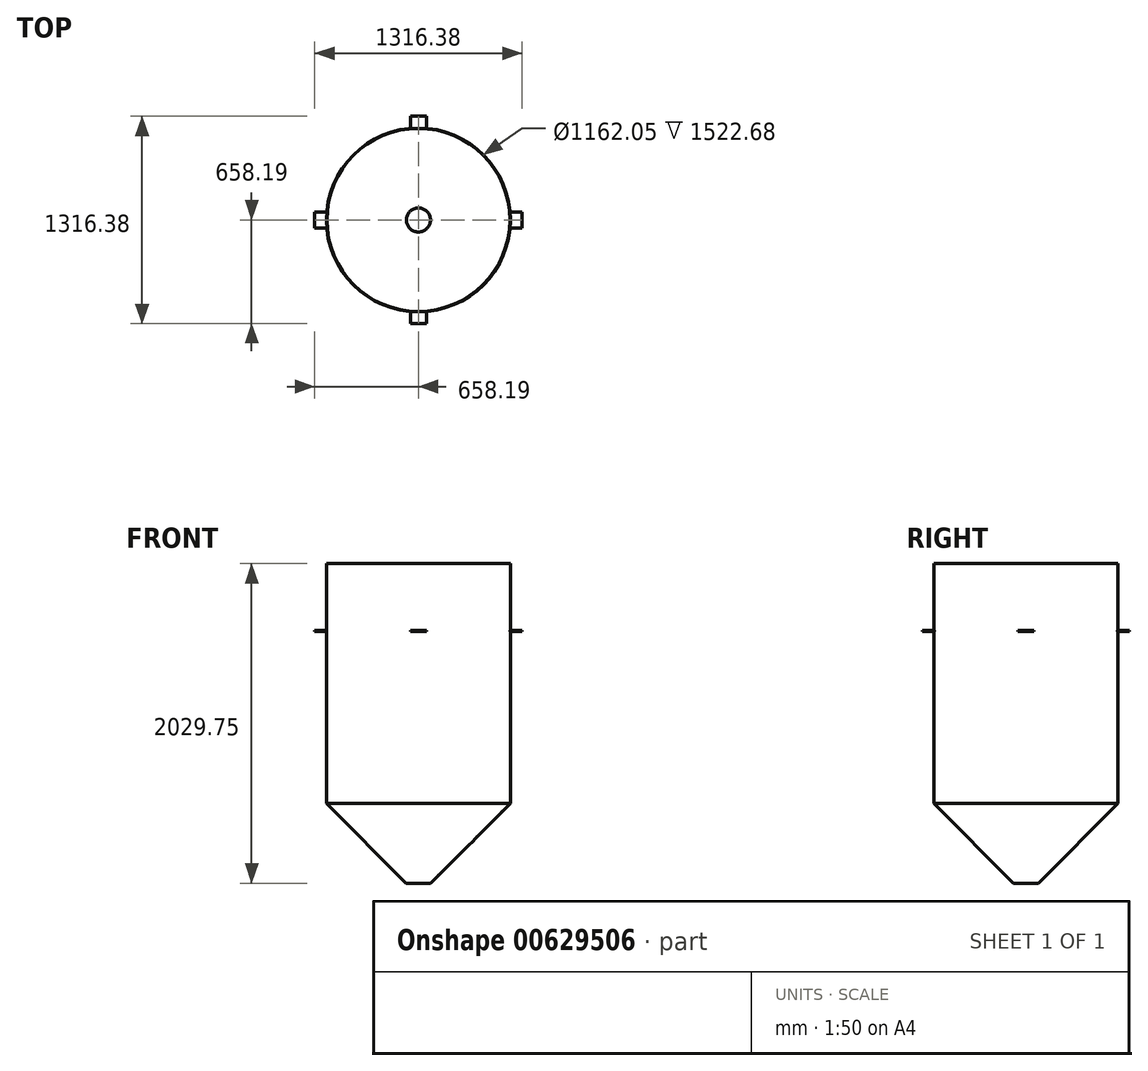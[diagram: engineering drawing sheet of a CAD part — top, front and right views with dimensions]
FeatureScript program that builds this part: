
annotation { "Feature Type Name" : "Feature", "Feature Type Description" : "" }
export const myFeature = defineFeature(function(context is Context, id is Id, definition is map)
    precondition{}
    {
        {
            var Q0;
            Q0=qCreatedBy(makeId("Right.planeOp"),FACE);
            var sketch = newSketch(context, id + "F0", { "sketchPlane" : qUnion([Q0])});
            skLineSegment(sketch, "E0", {"start": v(-584.2, 1524) * mm, "end": v(-584.2, 0) * mm});
            skLineSegment(sketch, "E1", {"start": v(-584.2, 0) * mm, "end": v(-78.45, -505.75) * mm});
            skLineSegment(sketch, "E2", {"start": v(-78.45, -505.75) * mm, "end": v(-76.2, -503.5) * mm});
            skLineSegment(sketch, "E3", {"start": v(-581.02, 1.32) * mm, "end": v(-581.02, 1524) * mm});
            skLineSegment(sketch, "E4", {"start": v(-581.02, 1524) * mm, "end": v(-584.2, 1524) * mm});
            skLineSegment(sketch, "E5", {"start": v(0, 139.51) * mm, "end": v(0, -139.51) * mm, "construction": true});
            skLineSegment(sketch, "E6", {"start": v(-76.2, -503.5) * mm, "end": v(-581.02, 1.32) * mm});
            skLineSegment(sketch, "E7", {"start": v(-78.45, -505.75) * mm, "end": v(0, -584.2) * mm, "construction": true});
            skSolve(sketch);
        }
        {
            var Q0;
            Q0=qSketchRegion(id+"F0",true);
            var Q1;
            Q1=sQuery(id+"F0.wireOp",EDGE,"E5");
            revolve(context, id + "F1", {"entities" : qUnion([Q0]), "axis" : qUnion([Q1]), "revolveType" : RevolveType.FULL});
        }
        {
            var Q0;
            Q0=qCreatedBy(makeId("Top.planeOp"),FACE);
            cPlane(context, id + "F2", {"entities" : qUnion([Q0]), "cplaneType" : CPlaneType.OFFSET, "offset" : 1092.2 * mm, "width" : 152.4 * mm, "height" : 152.4 * mm});
        }
        {
            var Q0;
            Q0=qCreatedBy(id+"F2.planeOp",FACE);
            var sketch = newSketch(context, id + "F3", { "sketchPlane" : qUnion([Q0])});
            skLineSegment(sketch, "E8.bottom", {"start": v(-50.8, 658.19) * mm, "end": v(50.8, 658.19) * mm});
            skLineSegment(sketch, "E8.top", {"start": v(-50.8, 581.99) * mm, "end": v(50.8, 581.99) * mm});
            skLineSegment(sketch, "E8.left", {"start": v(-50.8, 658.19) * mm, "end": v(-50.8, 581.99) * mm});
            skLineSegment(sketch, "E8.right", {"start": v(50.8, 658.19) * mm, "end": v(50.8, 581.99) * mm});
            skLineSegment(sketch, "E9", {"start": v(0, 581.99) * mm, "end": v(0, 0) * mm, "construction": true});
            skLineSegment(sketch, "E10.bottom", {"start": v(-658.19, 50.8) * mm, "end": v(-581.99, 50.8) * mm});
            skLineSegment(sketch, "E10.top", {"start": v(-658.19, -50.8) * mm, "end": v(-581.99, -50.8) * mm});
            skLineSegment(sketch, "E10.left", {"start": v(-658.19, 50.8) * mm, "end": v(-658.19, -50.8) * mm});
            skLineSegment(sketch, "E10.right", {"start": v(-581.99, 50.8) * mm, "end": v(-581.99, -50.8) * mm});
            skLineSegment(sketch, "E11.bottom", {"start": v(-50.8, -658.19) * mm, "end": v(50.8, -658.19) * mm});
            skLineSegment(sketch, "E11.top", {"start": v(-50.8, -581.99) * mm, "end": v(50.8, -581.99) * mm});
            skLineSegment(sketch, "E11.left", {"start": v(-50.8, -658.19) * mm, "end": v(-50.8, -581.99) * mm});
            skLineSegment(sketch, "E11.right", {"start": v(50.8, -658.19) * mm, "end": v(50.8, -581.99) * mm});
            skLineSegment(sketch, "E12.bottom", {"start": v(581.99, 50.8) * mm, "end": v(658.19, 50.8) * mm});
            skLineSegment(sketch, "E12.top", {"start": v(581.99, -50.8) * mm, "end": v(658.19, -50.8) * mm});
            skLineSegment(sketch, "E12.left", {"start": v(581.99, 50.8) * mm, "end": v(581.99, -50.8) * mm});
            skLineSegment(sketch, "E12.right", {"start": v(658.19, 50.8) * mm, "end": v(658.19, -50.8) * mm});
            skLineSegment(sketch, "E13", {"start": v(-581.99, 0) * mm, "end": v(0, 0) * mm, "construction": true});
            skLineSegment(sketch, "E14", {"start": v(581.99, 0) * mm, "end": v(0, 0) * mm, "construction": true});
            skLineSegment(sketch, "E15", {"start": v(0, -581.99) * mm, "end": v(0, 0) * mm, "construction": true});
            skSolve(sketch);
        }
        {
            var Q0;
            Q0=qSketchRegion(id+"F3",true);
            extrude(context, id + "F4", {"entities" : qUnion([Q0]), "operationType" : NewBodyOperationType.ADD, "depth" : 6.35 * mm});
        }
    });
